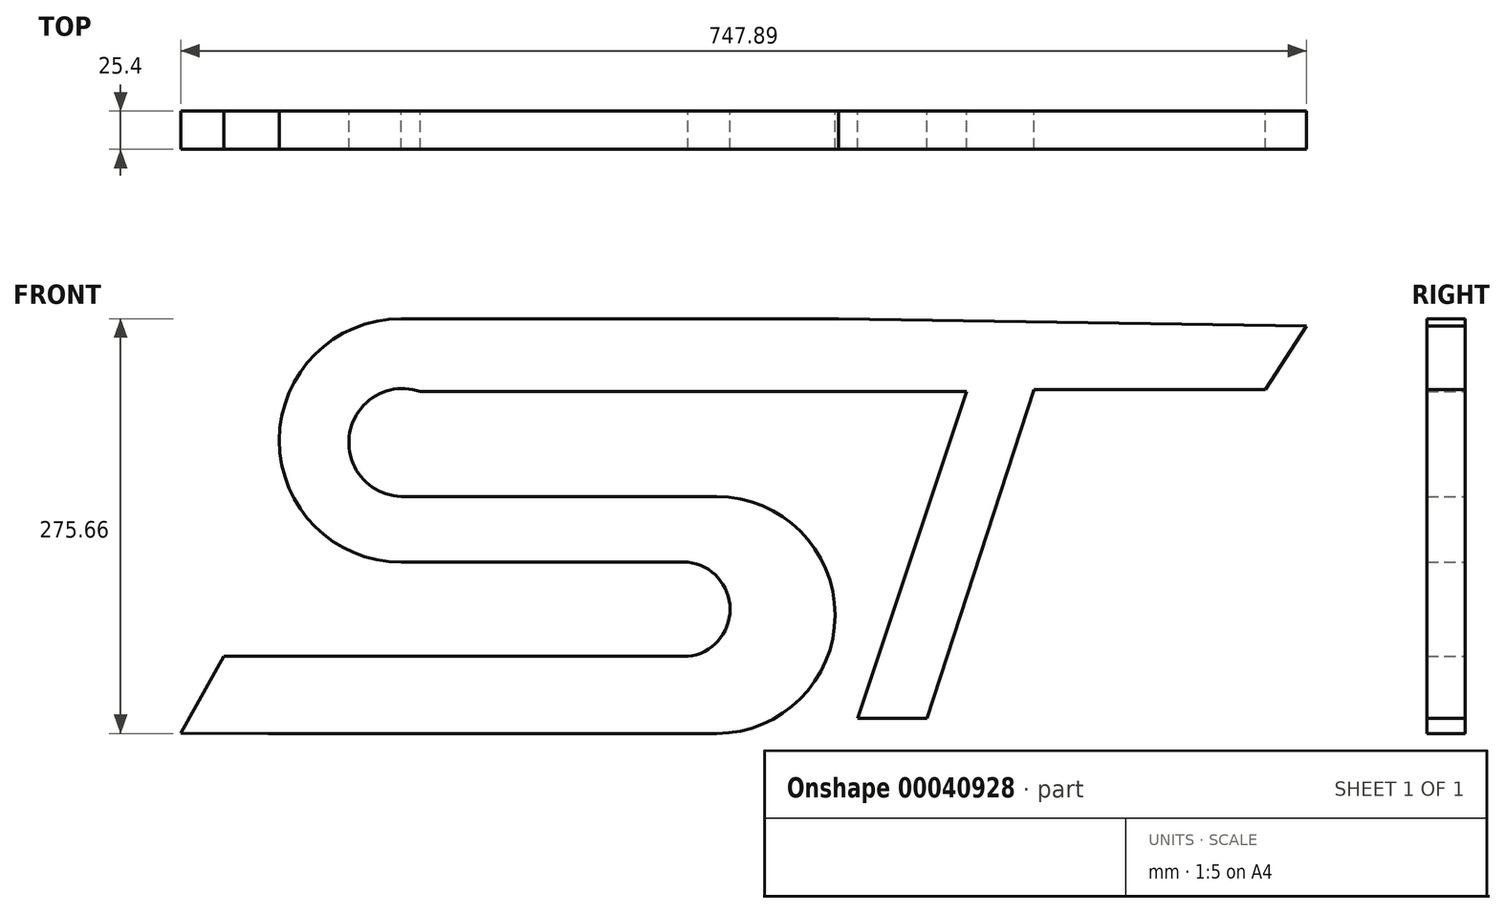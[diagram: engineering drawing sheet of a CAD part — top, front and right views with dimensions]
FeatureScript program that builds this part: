
annotation { "Feature Type Name" : "Feature", "Feature Type Description" : "" }
export const myFeature = defineFeature(function(context is Context, id is Id, definition is map)
    precondition{}
    {
        {
            var Q0;
            Q0=qCreatedBy(makeId("Front.planeOp"),FACE);
            var sketch = newSketch(context, id + "F0", { "sketchPlane" : qUnion([Q0])});
            skLineSegment(sketch, "E0", {"start": v(-227.9, -59.58) * mm, "end": v(-23, -59.58) * mm});
            skLineSegment(sketch, "E1", {"start": v(-23, -59.58) * mm, "end": v(69.98, -59.58) * mm});
            skArc(sketch, "E2", {"start": v(69.98, -59.58) * mm, "mid": v(148.72, 19.16) * mm, "end": v(69.98, 97.9) * mm});
            skPoint(sketch, "E2.second.point", {"position": v(69.98, 97.9) * mm});
            skPoint(sketch, "E2.third.point", {"position": v(87.06, 96.02) * mm});
            skLineSegment(sketch, "E3", {"start": v(-189.96, -8.35) * mm, "end": v(51, -8.35) * mm});
            skArc(sketch, "E4", {"start": v(43.93, -8.35) * mm, "mid": v(78.78, 19.42) * mm, "end": v(51, 54.26) * mm});
            skPoint(sketch, "E4.second.point", {"position": v(51, 54.26) * mm});
            skPoint(sketch, "E4.third.point", {"position": v(71.88, 42.87) * mm});
            skLineSegment(sketch, "E5", {"start": v(51, 54.26) * mm, "end": v(-139.5, 54.26) * mm});
            skLineSegment(sketch, "E6", {"start": v(69.98, 97.9) * mm, "end": v(-139.5, 97.9) * mm});
            skArc(sketch, "E7", {"start": v(-139.5, 216.08) * mm, "mid": v(-220.4, 135.17) * mm, "end": v(-139.5, 54.26) * mm});
            skPoint(sketch, "E7.second.point", {"position": v(-160.8, 213.22) * mm});
            skPoint(sketch, "E7.third.point", {"position": v(-139.5, 216.08) * mm});
            skArc(sketch, "E8", {"start": v(-118.24, 163.46) * mm, "mid": v(-172.82, 143.73) * mm, "end": v(-137.22, 97.9) * mm});
            skPoint(sketch, "E8.second.point", {"position": v(-118.24, 163.46) * mm});
            skPoint(sketch, "E8.third.point", {"position": v(-126.66, 167.67) * mm});
            skLineSegment(sketch, "E9", {"start": v(-139.5, 216.08) * mm, "end": v(151.14, 216.08) * mm});
            skLineSegment(sketch, "E10", {"start": v(-126.66, 167.67) * mm, "end": v(213.64, 167.67) * mm});
            skLineSegment(sketch, "E11", {"start": v(213.64, 167.67) * mm, "end": v(236.1, 167.67) * mm});
            skLineSegment(sketch, "E12", {"start": v(236.1, 167.67) * mm, "end": v(163.72, -49.5) * mm});
            skLineSegment(sketch, "E13", {"start": v(163.72, -49.5) * mm, "end": v(209.9, -49.5) * mm});
            skLineSegment(sketch, "E14", {"start": v(209.9, -49.5) * mm, "end": v(281.01, 168.85) * mm});
            skLineSegment(sketch, "E15", {"start": v(281.01, 168.85) * mm, "end": v(434.49, 168.85) * mm});
            skLineSegment(sketch, "E16", {"start": v(434.49, 168.85) * mm, "end": v(461.94, 211.27) * mm});
            skLineSegment(sketch, "E17", {"start": v(461.94, 211.27) * mm, "end": v(151.14, 216.08) * mm});
            skLineSegment(sketch, "E18", {"start": v(-189.96, -8.35) * mm, "end": v(-257.33, -8.35) * mm});
            skLineSegment(sketch, "E19", {"start": v(-257.33, -8.35) * mm, "end": v(-285.95, -59.33) * mm});
            skLineSegment(sketch, "E20", {"start": v(-285.95, -59.33) * mm, "end": v(-227.9, -59.58) * mm});
            skSolve(sketch);
        }
        {
            var Q0;
            Q0 = qSketchRegion(id + "F0", true);
            extrude(context, id + "F1", {"entities" : qUnion([Q0]), "depth" : 25.4 * mm});
        }
    });
